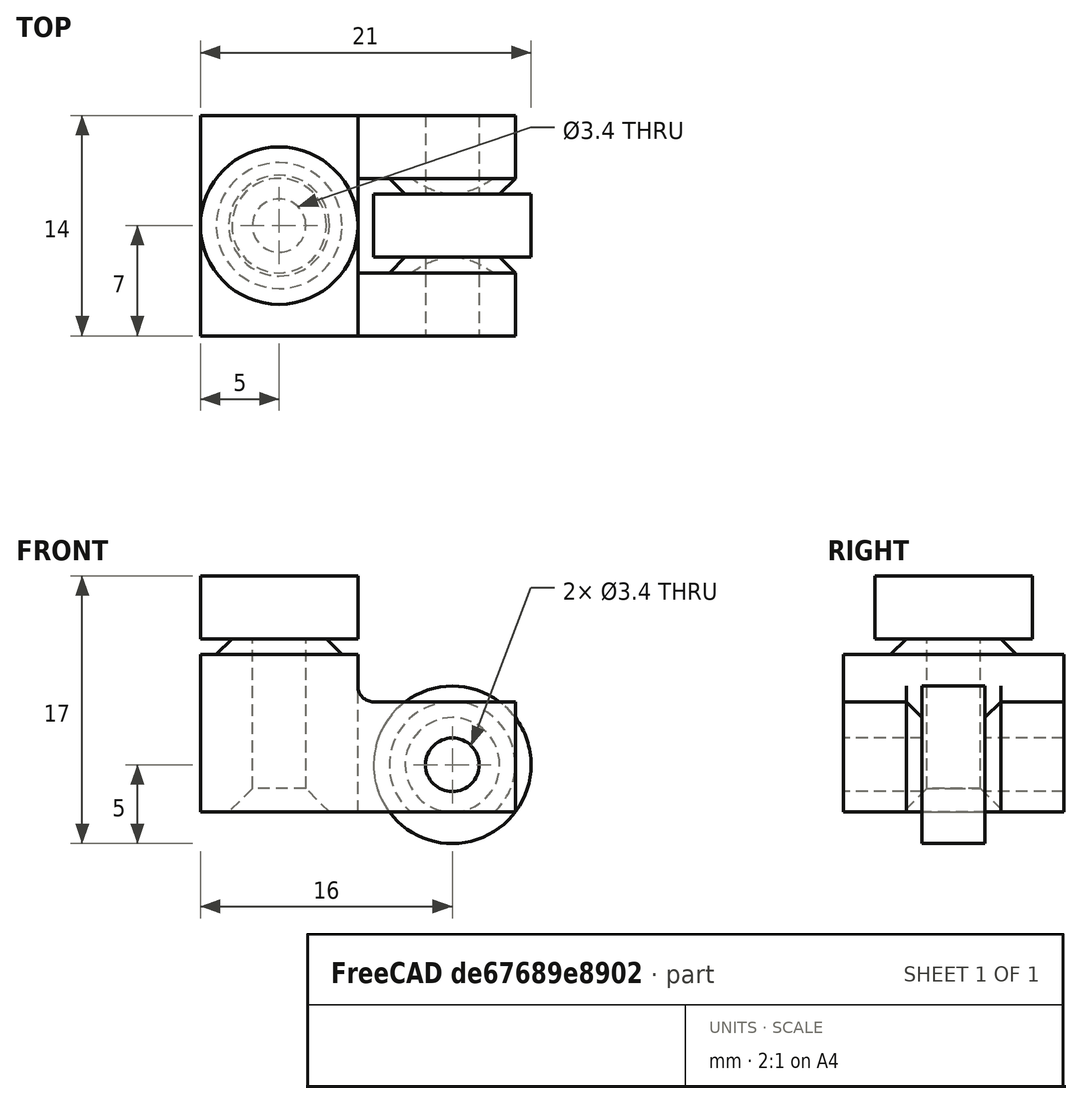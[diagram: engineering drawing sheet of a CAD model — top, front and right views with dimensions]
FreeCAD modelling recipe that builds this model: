
FCSTD DOCUMENT  (FreeCAD 0.18R16146 (Git))
Label: Castor 0.1
License: All rights reserved
LicenseURL: http://en.wikipedia.org/wiki/All_rights_reserved
objects: Part::Cylinder×4, Part::Box×4, Part::Cut×4, Part::Cone×3, Part::MultiFuse×3, Part::Fuse×1, Part::Chamfer×1, Part::Fillet×1
note: 21 computed .brp shape members not serialized (recipe doc carries the construction recipe); baked Part::Feature solids carry a one-line shape summary decoded from their .brp

FEATURE [Part::Cylinder] Cylinder082  label="623 Bearing"
  Angle = 360
  AttacherType = Attacher::AttachEngine3D
  Height = 4
  Placement = pos=(0,0,12) rot=(1,0,0;0rad)
  Radius = 5
FEATURE [Part::Cylinder] Cylinder083  label="623 Bearing001"
  Angle = 360
  AttacherType = Attacher::AttachEngine3D
  Height = 4
  Placement = pos=(11,2,4) rot=(1,0,0;1.5708rad)
  Radius = 5
FEATURE [Part::Cone] Cone
  Angle = 360
  AttacherType = Attacher::AttachEngine3D
  Height = 1
  Placement = pos=(0,0,12) rot=(1,0,0;3.14159rad)
  Radius1 = 3
  Radius2 = 4
FEATURE [Part::Box] Box  label="Cube"
  AttacherType = Attacher::AttachEngine3D
  Height = 10
  Length = 10
  Placement = pos=(-5,-7,1) rot=(0,0,1;0rad)
  Width = 14
FEATURE [Part::Box] Box001  label="Cube001"
  AttacherType = Attacher::AttachEngine3D
  Height = 7
  Length = 10
  Placement = pos=(5,-7,1) rot=(0,0,1;0rad)
  Width = 14
FEATURE [Part::Cone] Cone001
  Angle = 360
  AttacherType = Attacher::AttachEngine3D
  Height = 1
  Placement = pos=(11,-2,4) rot=(1,0,0;1.5708rad)
  Radius1 = 3
  Radius2 = 4
FEATURE [Part::Cone] Cone002
  Angle = 360
  AttacherType = Attacher::AttachEngine3D
  Height = 1
  Placement = pos=(11,2,4) rot=(-1,0,0;1.5708rad)
  Radius1 = 3
  Radius2 = 4
FEATURE [Part::Cylinder] Cylinder084  label="screw"
  Angle = 360
  AttacherType = Attacher::AttachEngine3D
  Height = 18
  Placement = pos=(11,8,4) rot=(1,0,0;1.5708rad)
  Radius = 1.7
FEATURE [Part::Box] Box002  label="Cube002"
  AttacherType = Attacher::AttachEngine3D
  Height = 10
  Length = 11
  Placement = pos=(5,-3,0) rot=(0,0,1;0rad)
  Width = 6
FEATURE [Part::Cut] Cut
  Base = -> Box001
  Tool = -> Box002
FEATURE [Part::Box] Box003  label="Cube003"
  AttacherType = Attacher::AttachEngine3D
  Height = 10
  Length = 10
  Placement = pos=(5,-5,-9) rot=(0,0,1;0rad)
  Width = 10
FEATURE [Part::Fuse] Fusion
  Base = -> Cone001
  Tool = -> Cone002
FEATURE [Part::Cut] Cut001
  Base = -> Fusion
  Tool = -> Box003
FEATURE [Part::MultiFuse] Fusion001
  Shapes = -> [Cut001,Cut]
FEATURE [Part::Cut] Cut002
  Base = -> Fusion001
  Tool = -> Cylinder084
FEATURE [Part::Cylinder] Cylinder
  Angle = 360
  AttacherType = Attacher::AttachEngine3D
  Height = 14
  Radius = 1.7
FEATURE [Part::MultiFuse] Fusion002
  Shapes = -> [Box,Cone]
FEATURE [Part::Cut] Cut003
  Base = -> Fusion002
  Tool = -> Cylinder
FEATURE [Part::MultiFuse] Fusion003
  Shapes = -> [Cut003,Cut002]
FEATURE [Part::Chamfer] Chamfer
  Base = -> Fusion003
  Edges = 1 edges r=1.5: [Edge18]
FEATURE [Part::Fillet] Fillet
  Base = -> Chamfer
  Edges = 2 edges r=1: [Edge25,Edge28]
